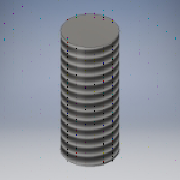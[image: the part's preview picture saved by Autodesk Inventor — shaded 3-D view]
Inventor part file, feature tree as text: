
AUTODESK INVENTOR PART (.ipt)
format: ipt  version: 2019 (Build 230136000, 136)  size: 118,784 bytes
history: native  units: mm
features: other x2, sketch x1, extrude x1, thread x1
ambient origin geometry x8: Origin, YZ Plane, XZ Plane, XY Plane, X Axis, Y Axis, Z Axis, Center Point
bodies: Body1 (feature_tree)
feature tree (5):
  other  "Bottom Plane"
  sketch  "Sketch1"  dims[d11=10.0mm d12=0.0mm d13=10.0mm d14=0.0mm]
  other  "Top Plane"
  extrude  "Extrusion2"  Depth=10.0mm TaperAngle=0.0deg
  thread  "Thread2"  [1 undecoded]
note: 1 required parameter value undecoded (feature->parameter linkage not recoverable at this tier; creation-order binding heuristic only, values carry confidence <= 0.55)
